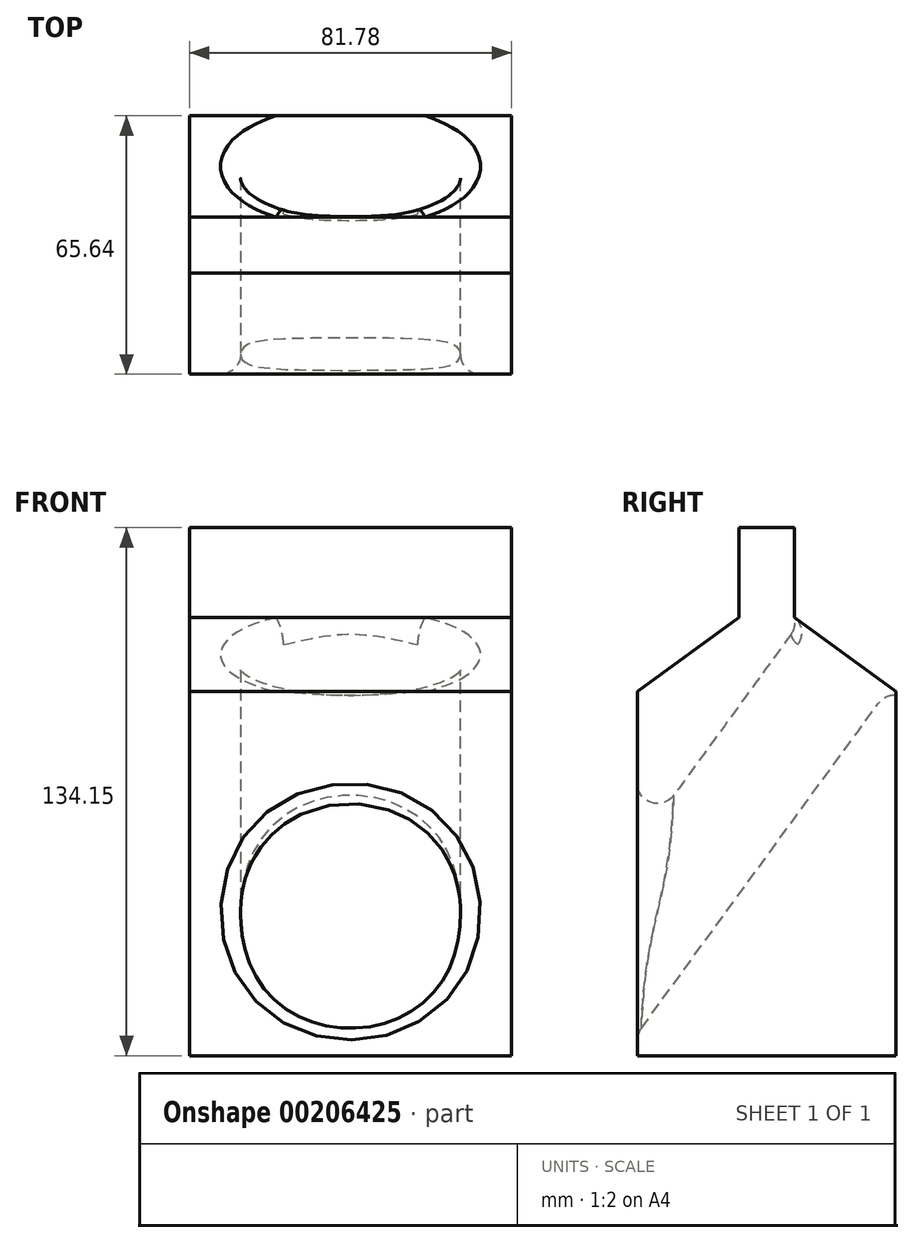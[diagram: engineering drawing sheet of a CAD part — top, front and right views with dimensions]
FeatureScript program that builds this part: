
annotation { "Feature Type Name" : "Feature", "Feature Type Description" : "" }
export const myFeature = defineFeature(function(context is Context, id is Id, definition is map)
    precondition{}
    {
        {
            var Q0;
            Q0=qCreatedBy(makeId("Right.planeOp"),FACE);
            var sketch = newSketch(context, id + "F0", { "sketchPlane" : qUnion([Q0])});
            skLineSegment(sketch, "E0.bottom", {"start": v(32.82, -80.8) * mm, "end": v(-32.82, -80.8) * mm});
            skLineSegment(sketch, "E0.top", {"start": v(32.82, 11.72) * mm, "end": v(-32.82, 11.72) * mm});
            skLineSegment(sketch, "E0.left", {"start": v(32.82, -80.8) * mm, "end": v(32.82, 11.72) * mm});
            skLineSegment(sketch, "E0.right", {"start": v(-32.82, -80.8) * mm, "end": v(-32.82, 11.72) * mm});
            skPoint(sketch, "E0.middle", {"position": v(0, -34.54) * mm});
            skLineSegment(sketch, "E1", {"start": v(32.82, 11.72) * mm, "end": v(7.08, 30.5) * mm});
            skLineSegment(sketch, "E2", {"start": v(7.08, 30.5) * mm, "end": v(7.08, 53.35) * mm});
            skLineSegment(sketch, "E3", {"start": v(7.08, 53.35) * mm, "end": v(0, 53.35) * mm});
            skLineSegment(sketch, "E4.MirrorCS", {"start": v(-7.08, 53.35) * mm, "end": v(0, 53.35) * mm});
            skLineSegment(sketch, "E5.MirrorCS", {"start": v(-7.08, 30.5) * mm, "end": v(-7.08, 53.35) * mm});
            skLineSegment(sketch, "E6.MirrorCS", {"start": v(-32.82, 11.72) * mm, "end": v(-7.08, 30.5) * mm});
            skSolve(sketch);
        }
        {
            var Q0;
            Q0=qCreatedBy(makeId("Right.planeOp"),FACE);
            var sketch = newSketch(context, id + "F1", { "sketchPlane" : qUnion([Q0])});
            skSolve(sketch);
        }
        {
            var Q0;
            Q0 = qSketchRegion(id + "F1", true);
            var Q1;
            Q1=makeQuery(id+"F0.imprint","IMPRINT",FACE,{"disambiguationData":[TD([[makeQuery(id+"F0.imprint","IMPRINT",EDGE,{"derivedFrom":sQuery(id+"F0.wireOp",EDGE,"E0.top")}),-1.0]])]});
            var Q2;
            Q2=makeQuery(id+"F0.imprint","IMPRINT",FACE,{"disambiguationData":[TD([[makeQuery(id+"F0.imprint","IMPRINT",EDGE,{"derivedFrom":sQuery(id+"F0.wireOp",EDGE,"E0.bottom")}),-1.0]])]});
            extrude(context, id + "F2", {"entities" : qUnion([Q0, Q1, Q2]), "endBound" : BoundingType.SYMMETRIC, "oppositeDirection" : true, "depth" : 50.8 * mm});
        }
        {
            var Q0;
            Q0=makeQuery(id+"F2.opExtrude","CAP_FACE",FACE,{"disambiguationData":[OSD([sQuery(id+"F0.wireOp",EDGE,"E0.bottom"),sQuery(id+"F0.wireOp",EDGE,"E0.left"),sQuery(id+"F0.wireOp",EDGE,"E0.right"),sQuery(id+"F0.wireOp",EDGE,"E1"),sQuery(id+"F0.wireOp",EDGE,"E2"),sQuery(id+"F0.wireOp",EDGE,"E3"),sQuery(id+"F0.wireOp",EDGE,"E4.MirrorCS"),sQuery(id+"F0.wireOp",EDGE,"E5.MirrorCS"),sQuery(id+"F0.wireOp",EDGE,"E6.MirrorCS")])],"isStart":false});
            var Q1;
            Q1=makeQuery(id+"F2.opExtrude","CAP_FACE",FACE,{"disambiguationData":[OSD([sQuery(id+"F0.wireOp",EDGE,"E0.bottom"),sQuery(id+"F0.wireOp",EDGE,"E0.left"),sQuery(id+"F0.wireOp",EDGE,"E0.right"),sQuery(id+"F0.wireOp",EDGE,"E1"),sQuery(id+"F0.wireOp",EDGE,"E2"),sQuery(id+"F0.wireOp",EDGE,"E3"),sQuery(id+"F0.wireOp",EDGE,"E4.MirrorCS"),sQuery(id+"F0.wireOp",EDGE,"E5.MirrorCS"),sQuery(id+"F0.wireOp",EDGE,"E6.MirrorCS")])],"isStart":true});
            extrude(context, id + "F3", {"entities" : qUnion([Q0, Q1]), "operationType" : NewBodyOperationType.ADD, "endBound" : BoundingType.SYMMETRIC, "depth" : 30.99 * mm});
        }
        {
            var Q0;
            {var subQ0=sQuery(id+"F0.wireOp",EDGE,"E1");Q0=makeQuery(id+"F3.boolean.opBoolean","MERGE",FACE,{"derivedFrom":[makeQuery(id+"F2.opExtrude","SWEPT_FACE",FACE,{"disambiguationData":[OSD([subQ0])]}),makeQuery(id+"F3.opExtrude","SWEPT_FACE",FACE,{"disambiguationData":[OSD([subQ0]),TDD([makeQuery(id+"F2.opExtrude","CAP_EDGE",EDGE,{"disambiguationData":[OSD([subQ0])],"isStart":true})])]}),makeQuery(id+"F3.opExtrude","SWEPT_FACE",FACE,{"disambiguationData":[OSD([subQ0]),TDD([makeQuery(id+"F2.opExtrude","CAP_EDGE",EDGE,{"disambiguationData":[OSD([subQ0])],"isStart":false})])]})]});}
            var sketch = newSketch(context, id + "F4", { "sketchPlane" : qUnion([Q0])});
            skEllipse(sketch, "E7", {"center": v(0, 3.67) * mm, "majorRadius": 27.93 * mm, "minorRadius": 14.13 * mm, "majorAxis": v(-1, 0)});
            skPoint(sketch, "E8.orphan", {"position": v(40.9, -12.26) * mm});
            skPoint(sketch, "E9.end.orphan", {"position": v(-40.9, 19.6) * mm});
            skSolve(sketch);
        }
        {
            var Q0;
            Q0 = qSketchRegion(id + "F4", true);
            extrude(context, id + "F5", {"entities" : qUnion([Q0]), "operationType" : NewBodyOperationType.REMOVE, "oppositeDirection" : true, "depth" : 144.02 * mm});
        }
        {
            var Q0;
            {var subQ0=sQuery(id+"F0.wireOp",EDGE,"E0.right");Q0=makeQuery(id+"F5.boolean.opBoolean","INTERSECT",EDGE,{"derivedFrom":[makeQuery(id+"F3.boolean.opBoolean","MERGE",FACE,{"derivedFrom":[makeQuery(id+"F2.opExtrude","SWEPT_FACE",FACE,{"disambiguationData":[OSD([subQ0])]}),makeQuery(id+"F3.opExtrude","SWEPT_FACE",FACE,{"disambiguationData":[OSD([subQ0]),TDD([makeQuery(id+"F2.opExtrude","CAP_EDGE",EDGE,{"disambiguationData":[OSD([subQ0])],"isStart":true})])]}),makeQuery(id+"F3.opExtrude","SWEPT_FACE",FACE,{"disambiguationData":[OSD([subQ0]),TDD([makeQuery(id+"F2.opExtrude","CAP_EDGE",EDGE,{"disambiguationData":[OSD([subQ0])],"isStart":false})])]})]}),makeQuery(id+"F5.opExtrude","SWEPT_FACE",FACE,{"disambiguationData":[OSD([sQuery(id+"F4.wireOp",EDGE,"E7")])]})]});}
            var Q1;
            Q1=makeQuery(id+"F5.boolean.opBoolean","COPY",FACE,{"derivedFrom":makeQuery(id+"F5.opExtrude","SWEPT_FACE",FACE,{"disambiguationData":[OSD([sQuery(id+"F4.wireOp",EDGE,"E7")])]})});
            fillet(context, id + "F6", {"entities" : qUnion([Q0, Q1]), "radius" : 5.08 * mm, "tangentPropagation" : true, "allowEdgeOverflow" : false});
        }
    });
